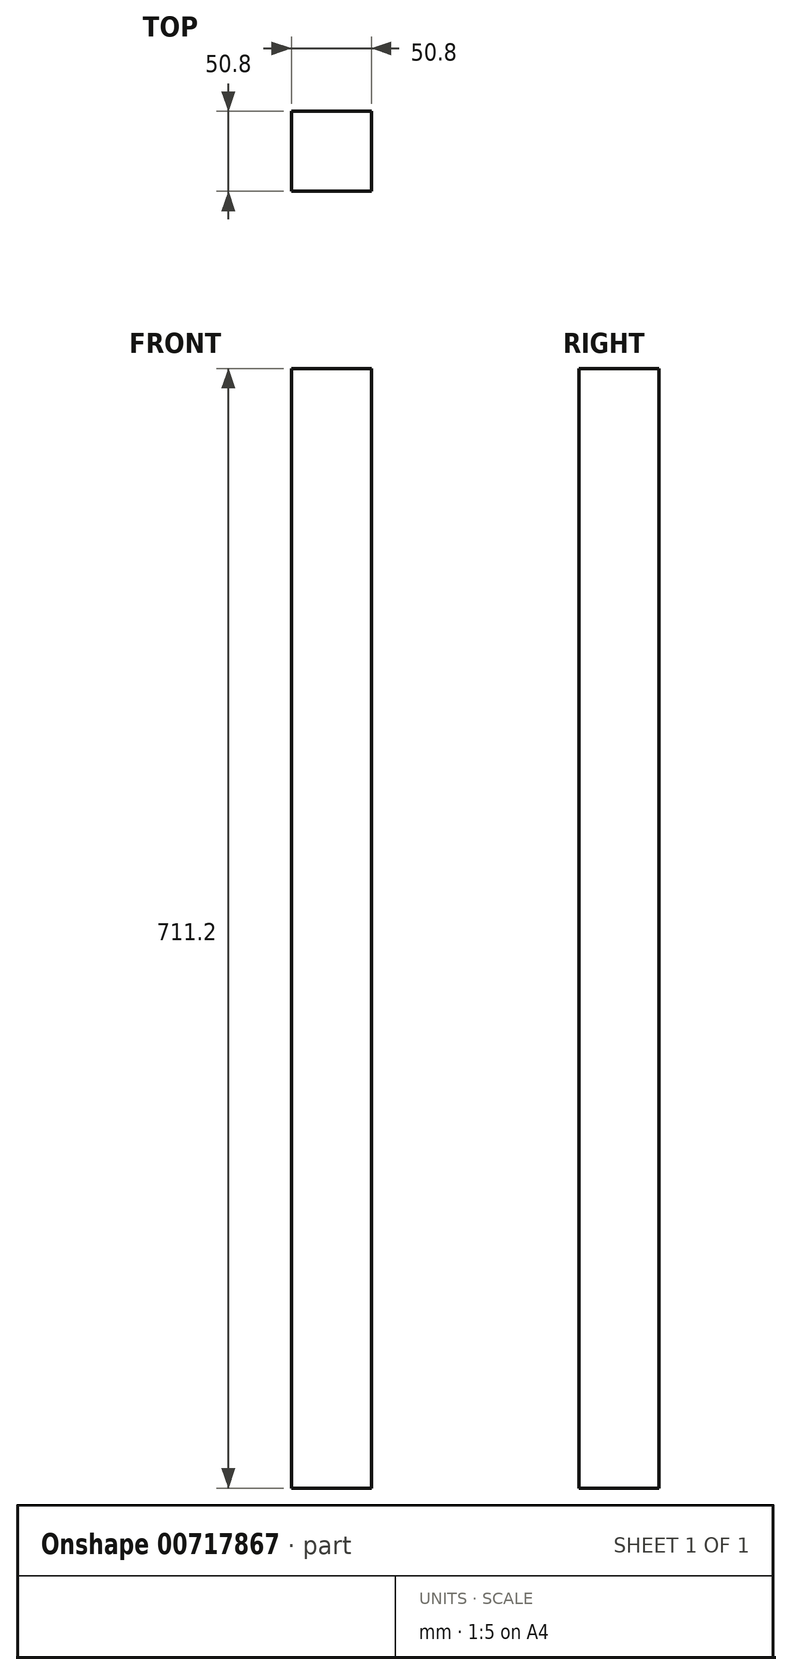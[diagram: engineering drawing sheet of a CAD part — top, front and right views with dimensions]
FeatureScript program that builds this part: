
annotation { "Feature Type Name" : "Feature", "Feature Type Description" : "" }
export const myFeature = defineFeature(function(context is Context, id is Id, definition is map)
    precondition{}
    {
        {
            var Q0;
            Q0=qCreatedBy(makeId("Top.planeOp"),FACE);
            var sketch = newSketch(context, id + "F0", { "sketchPlane" : qUnion([Q0])});
            skLineSegment(sketch, "E0.bottom", {"start": v(25.4, 25.4) * mm, "end": v(-25.4, 25.4) * mm});
            skLineSegment(sketch, "E0.top", {"start": v(25.4, -25.4) * mm, "end": v(-25.4, -25.4) * mm});
            skLineSegment(sketch, "E0.left", {"start": v(25.4, 25.4) * mm, "end": v(25.4, -25.4) * mm});
            skLineSegment(sketch, "E0.right", {"start": v(-25.4, 25.4) * mm, "end": v(-25.4, -25.4) * mm});
            skPoint(sketch, "E0.middle", {"position": v(0, 0) * mm});
            skSolve(sketch);
        }
        {
            var Q0;
            Q0 = qSketchRegion(id + "F0", true);
            extrude(context, id + "F1", {"entities" : qUnion([Q0]), "depth" : 711.2 * mm, "offsetDistance" : 25.4 * mm});
        }
    });
